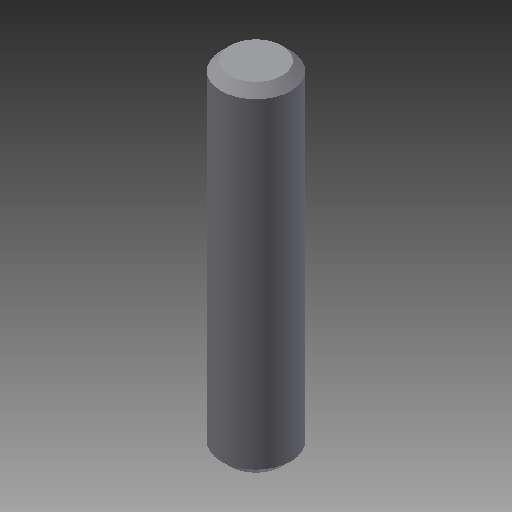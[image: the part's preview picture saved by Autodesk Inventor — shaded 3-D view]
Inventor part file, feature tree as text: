
AUTODESK INVENTOR PART (.ipt)
format: ipt  version: 2019 (Build 230136000, 136)  size: 96,768 bytes
history: native  units: in
note: dims shown in document units (in); Inventor stores cm internally (conversion verified against a paired STEP export)
features: other x7, revolve x1, sketch x1
ambient origin geometry x8: Origin, YZ Plane, XZ Plane, XY Plane, X Axis, Y Axis, Z Axis, Center Point
bodies: Solid1 (feature_tree)
feature tree (9):
  revolve  "Revolution1"  [1 undecoded]
  other  "to_a_XY"
  other  "to_a_YZ"
  other  "to_a_ZX"
  other  "to_a_X"
  other  "to_a_Y"
  other  "to_a_Z"
  other  "to_a_Center"
  sketch  "Sketch_1"  dims[d0=360.0deg]
note: 1 required parameter value undecoded (feature->parameter linkage not recoverable at this tier; creation-order binding heuristic only, values carry confidence <= 0.55)
